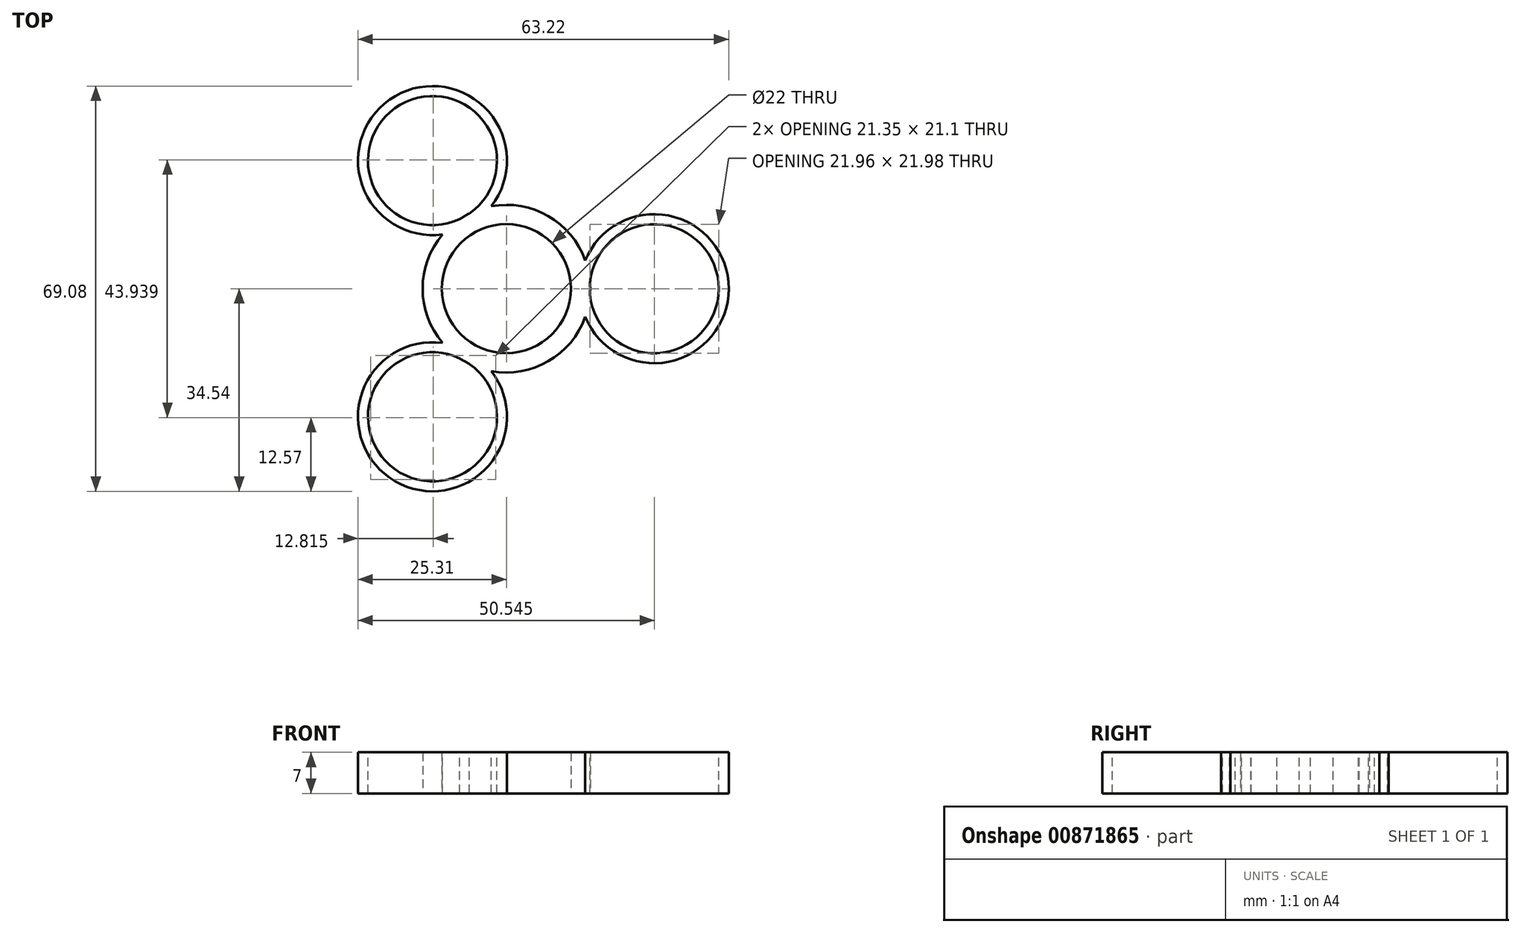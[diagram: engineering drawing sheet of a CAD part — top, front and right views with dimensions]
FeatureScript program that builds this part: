
annotation { "Feature Type Name" : "Feature", "Feature Type Description" : "" }
export const myFeature = defineFeature(function(context is Context, id is Id, definition is map)
    precondition{}
    {
        {
            var Q0;
            Q0=qCreatedBy(makeId("Top.planeOp"),FACE);
            var sketch = newSketch(context, id + "F0", { "sketchPlane" : qUnion([Q0])});
            skCircle(sketch, "E0", {"center": v(0, 0) * mm, "radius": 11 * mm});
            skCircle(sketch, "E1", {"center": v(0, 0) * mm, "radius": 14.29 * mm});
            skSolve(sketch);
        }
        {
            var Q0;
            Q0=makeQuery(id+"F0.imprint","IMPRINT",FACE,{"disambiguationData":[TD([[makeQuery(id+"F0.imprint","IMPRINT",EDGE,{"derivedFrom":sQuery(id+"F0.wireOp",EDGE,"E0")}),-1.0]])]});
            extrude(context, id + "F1", {"entities" : qUnion([Q0]), "depth" : 7 * mm, "offsetDistance" : 25.4 * mm});
        }
        {
            var Q0;
            Q0=makeQuery(id+"F1.opExtrude","CAP_FACE",FACE,{"disambiguationData":[OSD([sQuery(id+"F0.wireOp",EDGE,"E0"),sQuery(id+"F0.wireOp",EDGE,"E1")])],"isStart":false});
            var sketch = newSketch(context, id + "F2", { "sketchPlane" : qUnion([Q0])});
            skCircle(sketch, "E2", {"center": v(25.21, 0) * mm, "radius": 11 * mm});
            skCircle(sketch, "E3", {"center": v(25.21, 0) * mm, "radius": 12.7 * mm});
            skSolve(sketch);
        }
        {
            var Q0;
            {var subQ0=sQuery(id+"F2.wireOp",EDGE,"E2");var subQ1=makeQuery(id+"F1.opExtrude","CAP_EDGE",EDGE,{"disambiguationData":[OSD([sQuery(id+"F0.wireOp",EDGE,"E1")])],"isStart":false});var subQ2=makeQuery(id+"F2.imprint","INTERSECT",VERTEX,{"disambiguationData":[OD(0.0)],"derivedFrom":[subQ1,subQ0]});Q0=makeQuery(id+"F2.imprint","IMPRINT",FACE,{"disambiguationData":[TD([[makeQuery(id+"F2.imprint","IMPRINT",EDGE,{"disambiguationData":[TD([[subQ2,-1.0]])],"derivedFrom":subQ0}),-1.0]])]});}
            extrude(context, id + "F3", {"entities" : qUnion([Q0]), "operationType" : NewBodyOperationType.ADD, "oppositeDirection" : true, "depth" : 7 * mm, "offsetDistance" : 25.4 * mm});
        }
        {
            var Q0;
            Q0=makeQuery(id+"F1.opExtrude","SWEPT_BODY",BODY,{"disambiguationData":[OSD([sQuery(id+"F0.wireOp",EDGE,"E0"),sQuery(id+"F0.wireOp",EDGE,"E1")])]});
            var Q1;
            Q1=makeQuery(id+"F1.opExtrude","CAP_EDGE",EDGE,{"disambiguationData":[OSD([sQuery(id+"F0.wireOp",EDGE,"E0")])],"isStart":false});
            circularPattern(context, id + "F4", {"operationType" : NewBodyOperationType.ADD, "entities" : qUnion([Q0]), "axis" : qUnion([Q1]), "angle" : 360 * degree, "instanceCount" : 3, "equalSpace" : true});
        }
    });
